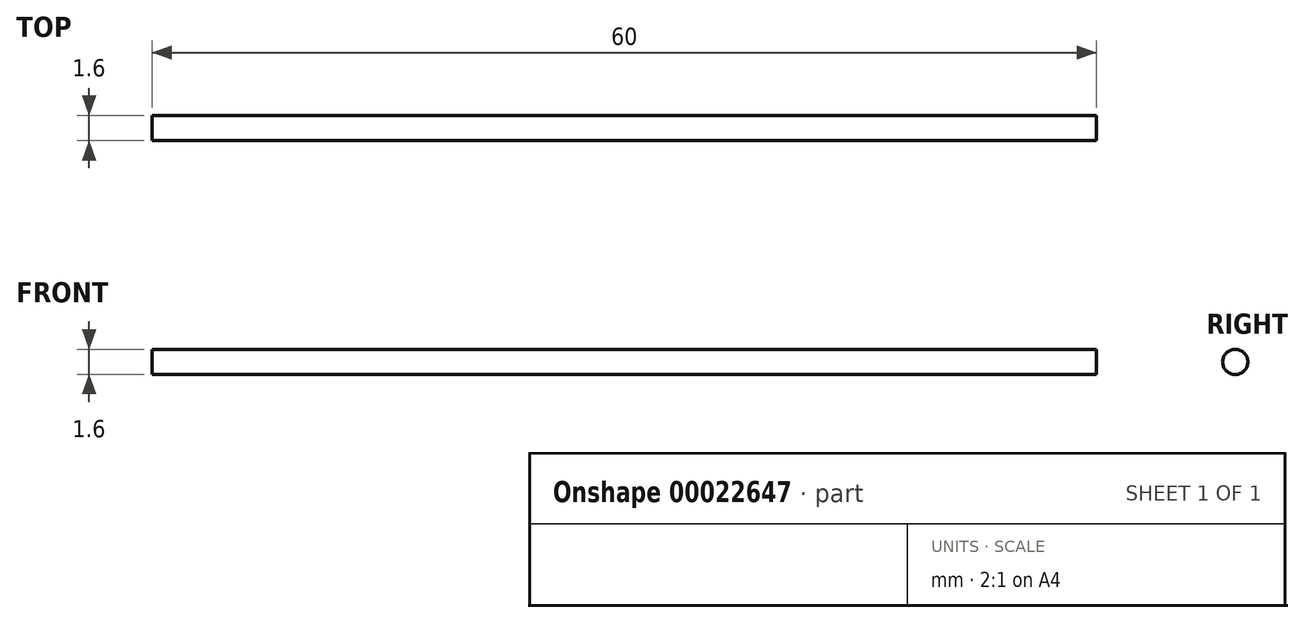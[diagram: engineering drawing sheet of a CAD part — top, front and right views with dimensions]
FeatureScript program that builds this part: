
annotation { "Feature Type Name" : "Feature", "Feature Type Description" : "" }
export const myFeature = defineFeature(function(context is Context, id is Id, definition is map)
    precondition{}
    {
        {
            var Q0;
            Q0=qCreatedBy(makeId("Front.planeOp"),FACE);
            var sketch = newSketch(context, id + "F0", { "sketchPlane" : qUnion([Q0])});
            skLineSegment(sketch, "E0.bottom", {"start": v(-16.48, 18.4) * mm, "end": v(43.52, 18.4) * mm});
            skLineSegment(sketch, "E0.top", {"start": v(-16.48, 17.6) * mm, "end": v(43.52, 17.6) * mm});
            skLineSegment(sketch, "E0.left", {"start": v(-16.48, 18.4) * mm, "end": v(-16.48, 17.6) * mm});
            skLineSegment(sketch, "E0.right", {"start": v(43.52, 18.4) * mm, "end": v(43.52, 17.6) * mm});
            skSolve(sketch);
        }
        {
            var Q0;
            Q0=makeQuery(id+"F0.imprint","IMPRINT",FACE,{"disambiguationData":[TD([[makeQuery(id+"F0.imprint","IMPRINT",EDGE,{"derivedFrom":sQuery(id+"F0.wireOp",EDGE,"E0.bottom")}),-1.0]])]});
            var Q1;
            Q1=sQuery(id+"F0.wireOp",EDGE,"E0.top");
            revolve(context, id + "F1", {"entities" : qUnion([Q0]), "axis" : qUnion([Q1]), "revolveType" : RevolveType.FULL});
        }
    });
